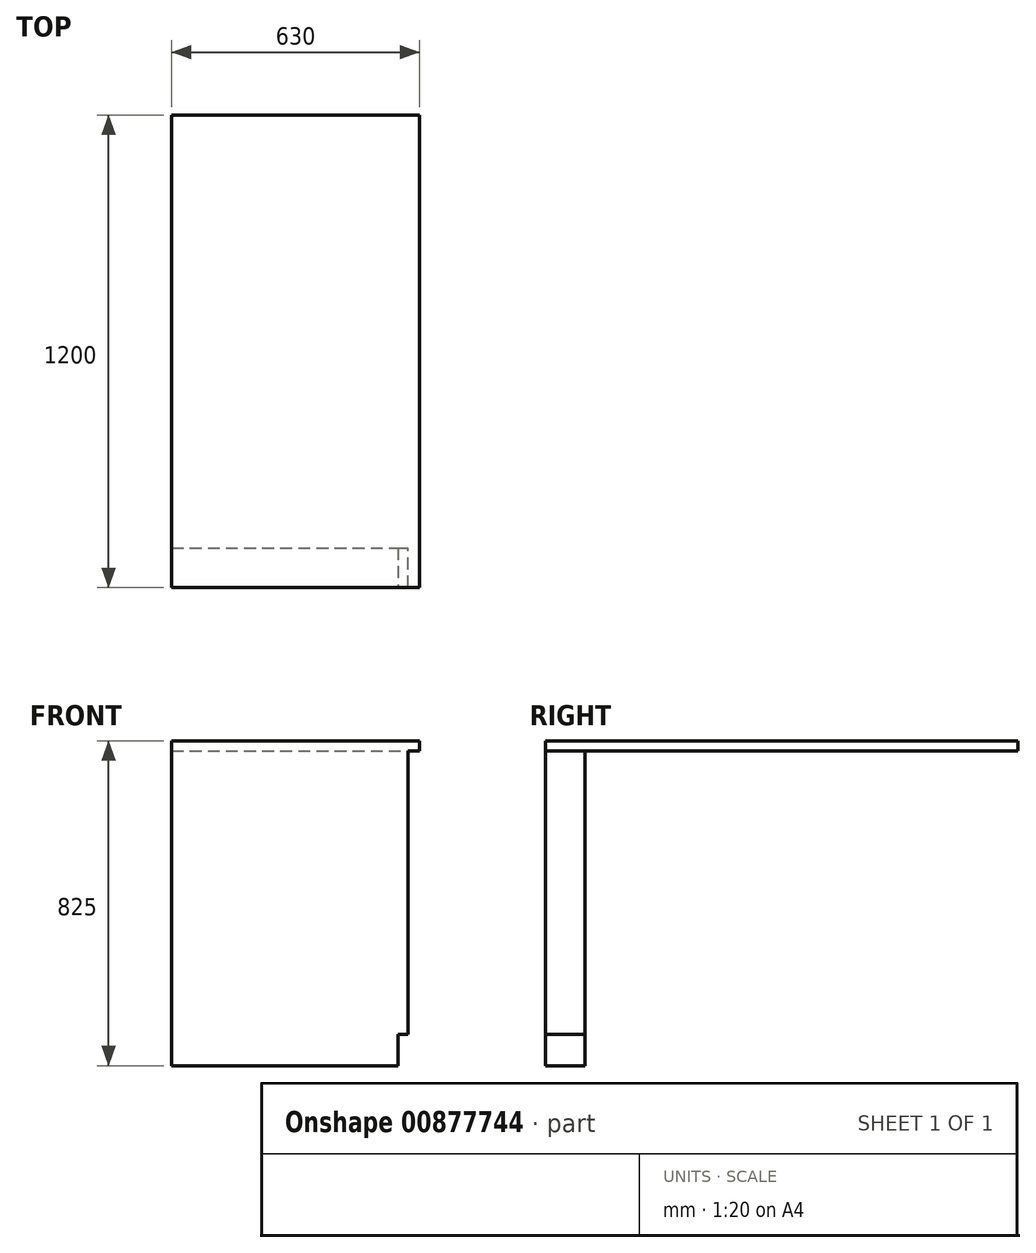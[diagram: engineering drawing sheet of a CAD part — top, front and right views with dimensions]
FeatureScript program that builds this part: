
annotation { "Feature Type Name" : "Feature", "Feature Type Description" : "" }
export const myFeature = defineFeature(function(context is Context, id is Id, definition is map)
    precondition{}
    {
        {
            var Q0;
            Q0=qCreatedBy(makeId("Top.planeOp"),FACE);
            var sketch = newSketch(context, id + "F0", { "sketchPlane" : qUnion([Q0])});
            skLineSegment(sketch, "E0.bottom", {"start": v(-300, 50) * mm, "end": v(300, 50) * mm});
            skLineSegment(sketch, "E0.top", {"start": v(-300, -50) * mm, "end": v(300, -50) * mm});
            skLineSegment(sketch, "E0.left", {"start": v(-300, 50) * mm, "end": v(-300, -50) * mm});
            skLineSegment(sketch, "E0.right", {"start": v(300, 50) * mm, "end": v(300, -50) * mm});
            skPoint(sketch, "E0.middle", {"position": v(0, 0) * mm});
            skSolve(sketch);
        }
        {
            var Q0;
            Q0=qSketchRegion(id+"F0",true);
            extrude(context, id + "F1", {"entities" : qUnion([Q0]), "depth" : 800 * mm, "offsetDistance" : 25 * mm});
        }
        {
            var Q0;
            Q0=makeQuery(id+"F1.opExtrude","SWEPT_FACE",FACE,{"disambiguationData":[OSD([sQuery(id+"F0.wireOp",EDGE,"E0.right")])]});
            var sketch = newSketch(context, id + "F2", { "sketchPlane" : qUnion([Q0])});
            skLineSegment(sketch, "E1.bottom", {"start": v(-50, 0) * mm, "end": v(50, 0) * mm});
            skLineSegment(sketch, "E1.top", {"start": v(-50, 80) * mm, "end": v(50, 80) * mm});
            skLineSegment(sketch, "E1.left", {"start": v(-50, 0) * mm, "end": v(-50, 80) * mm});
            skLineSegment(sketch, "E1.right", {"start": v(50, 0) * mm, "end": v(50, 80) * mm});
            skSolve(sketch);
        }
        {
            var Q0;
            Q0=qSketchRegion(id+"F2",true);
            extrude(context, id + "F3", {"entities" : qUnion([Q0]), "operationType" : NewBodyOperationType.REMOVE, "oppositeDirection" : true, "depth" : 25 * mm, "offsetDistance" : 25 * mm});
        }
        {
            var Q0;
            Q0=makeQuery(id+"F1.opExtrude","CAP_FACE",FACE,{"disambiguationData":[OSD([sQuery(id+"F0.wireOp",EDGE,"E0.bottom"),sQuery(id+"F0.wireOp",EDGE,"E0.top"),sQuery(id+"F0.wireOp",EDGE,"E0.left"),sQuery(id+"F0.wireOp",EDGE,"E0.right")])],"isStart":false});
            var sketch = newSketch(context, id + "F4", { "sketchPlane" : qUnion([Q0])});
            skLineSegment(sketch, "E2.bottom", {"start": v(-300, -50) * mm, "end": v(330, -50) * mm});
            skLineSegment(sketch, "E2.top", {"start": v(-300, 50) * mm, "end": v(330, 50) * mm});
            skLineSegment(sketch, "E2.left", {"start": v(-300, -50) * mm, "end": v(-300, 50) * mm});
            skLineSegment(sketch, "E2.right", {"start": v(330, -50) * mm, "end": v(330, 50) * mm});
            skSolve(sketch);
        }
        {
            var Q0;
            Q0=qSketchRegion(id+"F4",true);
            extrude(context, id + "F5", {"entities" : qUnion([Q0]), "operationType" : NewBodyOperationType.ADD, "depth" : 25 * mm, "offsetDistance" : 25 * mm});
        }
        {
            var Q0;
            Q0=makeQuery(id+"F5.boolean.opBoolean","MERGE",FACE,{"derivedFrom":[makeQuery(id+"F1.opExtrude","SWEPT_FACE",FACE,{"disambiguationData":[OSD([sQuery(id+"F0.wireOp",EDGE,"E0.bottom")])]}),makeQuery(id+"F5.opExtrude","SWEPT_FACE",FACE,{"disambiguationData":[OSD([sQuery(id+"F4.wireOp",EDGE,"E2.top")])]})]});
            var sketch = newSketch(context, id + "F6", { "sketchPlane" : qUnion([Q0])});
            skLineSegment(sketch, "E3.bottom", {"start": v(-330, 800) * mm, "end": v(300, 800) * mm});
            skLineSegment(sketch, "E3.top", {"start": v(-330, 825) * mm, "end": v(300, 825) * mm});
            skLineSegment(sketch, "E3.left", {"start": v(-330, 800) * mm, "end": v(-330, 825) * mm});
            skLineSegment(sketch, "E3.right", {"start": v(300, 800) * mm, "end": v(300, 825) * mm});
            skSolve(sketch);
        }
        {
            var Q0;
            Q0=qSketchRegion(id+"F6",true);
            extrude(context, id + "F7", {"entities" : qUnion([Q0]), "operationType" : NewBodyOperationType.ADD, "depth" : 1100 * mm, "offsetDistance" : 25 * mm});
        }
    });
